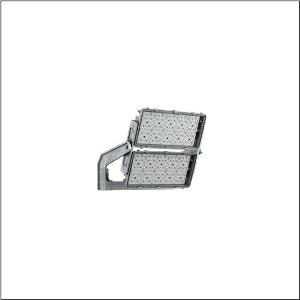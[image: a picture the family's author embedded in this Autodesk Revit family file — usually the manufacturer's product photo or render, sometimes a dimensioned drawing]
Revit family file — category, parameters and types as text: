
# Revit family: floodlight_fl_11_maxi_remote___rs12_5xa779514m01ba_3a09
name_source: partatom
category: Lighting Fixtures
units: mm (PartAtom-declared; Revit-internal decimal feet)

## family parameters
Cut with Voids When Loaded = No
Host = Face
Light Source = No
Part Type = Normal
Room Calculation Point = No
Round Connector Dimension = Use Diameter
Shared = No

## types (1)
- --- (1 x LED, 76660 lm, 707.9 W, 5700K)
    Apparent Load = 708 VA
    CIE Flux Codes = 79 92 99 100 100
    Color Rendering = 90
    Color Temperature = 5700K
    Default Elevation = 1800 mm
    Description = Floodlight FL 11  maxi  Remote floodlight; light control with lens of PMMA; cover panel of toughened safety glass, transparent; light distribution: RS12, rotationally symmetric direct distribution, LEDcolour temperature: 5700K, rated luminous flux: 76.660lm, colour rendering: CRI > 90, light colour: 957; luminous efficacy: 108lm/W; brightness control: DMX+RDM; with terminal, 8-pole, max. 2.5mm², mains connection: 220..240V/380..400V AC, 50/60Hz, surge voltage resistance: line to ground: 10kV, ECG replaceable separately, LED unit replaceable without ESD environment, dustproof LED module, dimming range 10..100%; 708W floodlight with 2x LED unit of diecast aluminium, coated grey; length: 713mm / width: 651mm / height: 338mm; mounting bracket, of diecast aluminium, uncoated, natural, equipment: Longlife, protection rating (complete): IP66; insulation class (complete): insulation class I (protective earthing); certification: CE, ENEC, VDE; ball protection: ball impact resistance with accessories, impact resistance: IK07; only for outdoor installations, rated ambient temperature 10°C, permissible operating ambient temperature: -40..+40°C, permissible storage temperature: -40..+85°C; packaging unit: 1 piece

Light Distribution: RS12
    Height = 320 mm
    Lamp = 1 x LED
    Lamp Light Flux = 76660 lm
    Lamp Power = 707.9 W
    Lamp count = 1
    Length = 712 mm
    Luminous efficacy = 108 lm/W
    Manufacturer = Siteco
    ModVariant = No
    Model = 5XA779514M01BA
    Mounting Place = Ceiling
    Mounting Type = Surface mounted
    Number of Poles = 1
    OnlyDefault = Yes
    Power Factor = 1
    Product Name = Floodlight FL 11 maxi Remote | RS12
    Product group = floodlight | ceiling mounted
    ProductGroupID = 302
    Protection Class = Protection class I
    Protection Degree = IP 66
    RLX_Detail_Level = 1
    RLX_Emergency_Light_Flux = 0 lm
    RLX_Emergency_Type = 0
    RLX_Emergency_Type_DB = No
    RlxData = <blob elided: 41105 chars, md5=ca2007a0>
    Socket = socket
    Standby Power = 0 W
    System Light Flux = 76660 lm
    System Power = 708 W
    Type Comments = factory setting: luminous flux: 100 % | dim-lin: 254 | 740 mA
    Type Image = l_1006788.jpg
    URL = http://relux.com
    VarID = @adj_115165
    Voltage = 0 V
    Weight = 0.00 kg
    Width = 655 mm

## geometry (parser evidence)
native form markers: Blend x4, Sweep x12
no freeform markers — native parametric forms only
